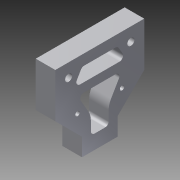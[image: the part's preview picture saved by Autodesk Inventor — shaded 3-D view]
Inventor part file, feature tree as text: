
AUTODESK INVENTOR PART (.ipt)
format: ipt  version: 2013 (Build 170138000, 138)  size: 254,464 bytes
history: native  units: mm
features: sketch x8, extrude x6, hole x2, fillet x2, other x1, pattern_circular x1
ambient origin geometry x8: Origin, YZ Plane, XZ Plane, XY Plane, X Axis, Y Axis, Z Axis, Center Point
feature tree (20):
  other  "ソリッド1"
  extrude  "押し出し1"  Depth=100.0mm
  extrude  "押し出し2"  Depth=100.0mm
  extrude  "押し出し5"  Depth=50.0mm
  hole  "穴1"  [1 undecoded]
  pattern_circular  "円形状パターン2"  [2 undecoded]
  hole  "穴2"  [1 undecoded]
  extrude  "押し出し6"  TaperAngle=135.0deg  [1 undecoded]
  sketch  "スケッチ7"
  sketch  "スケッチ8"
  extrude  "押し出し11"  Depth=25.0mm
  extrude  "押し出し12"  Depth=25.0mm
  fillet  "フィレット1"  Radius=50.0mm
  fillet  "フィレット2"  [1 undecoded]
  sketch  "スケッチ1"
  sketch  "スケッチ2"
  sketch  "スケッチ3"
  sketch  "スケッチ4"
  sketch  "スケッチ5"
  sketch  "スケッチ6"
note: 6 required parameter values undecoded (feature->parameter linkage not recoverable at this tier; creation-order binding heuristic only, values carry confidence <= 0.55)
